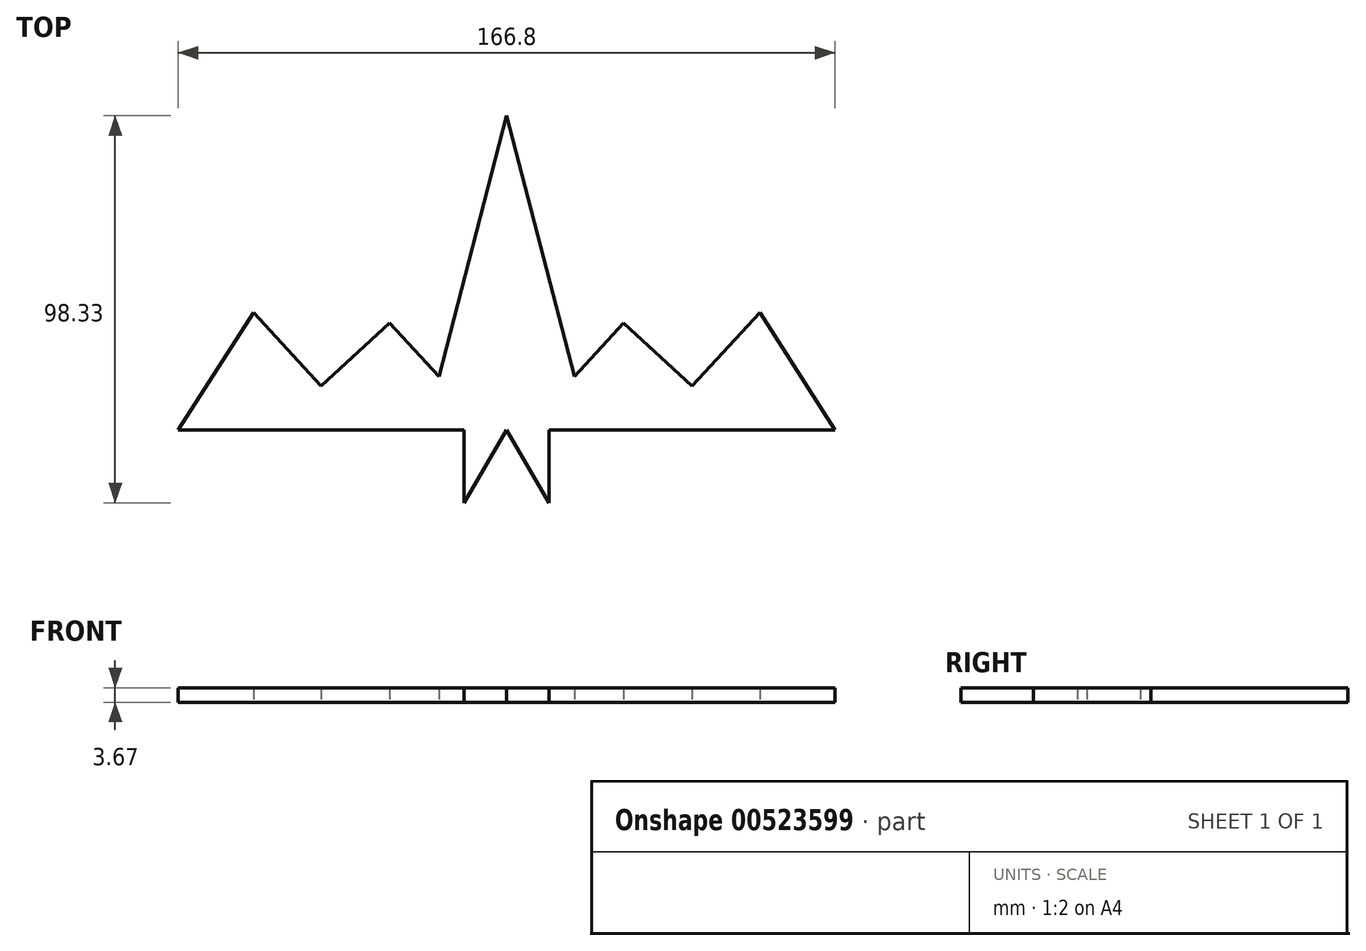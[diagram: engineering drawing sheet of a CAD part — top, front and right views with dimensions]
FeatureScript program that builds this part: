
annotation { "Feature Type Name" : "Feature", "Feature Type Description" : "" }
export const myFeature = defineFeature(function(context is Context, id is Id, definition is map)
    precondition{}
    {
        {
            var Q0;
            Q0=qCreatedBy(makeId("Top.planeOp"),FACE);
            var sketch = newSketch(context, id + "F0", { "sketchPlane" : qUnion([Q0])});
            skLineSegment(sketch, "E0", {"start": v(0, -45.85) * mm, "end": v(-10.79, -64.31) * mm});
            skLineSegment(sketch, "E1", {"start": v(-10.79, -64.31) * mm, "end": v(-10.79, -45.85) * mm});
            skLineSegment(sketch, "E2", {"start": v(-10.79, -45.85) * mm, "end": v(-83.4, -45.85) * mm});
            skLineSegment(sketch, "E3", {"start": v(-83.4, -45.85) * mm, "end": v(-64.31, -15.97) * mm});
            skLineSegment(sketch, "E4", {"start": v(-64.31, -15.97) * mm, "end": v(-47.1, -34.65) * mm});
            skPoint(sketch, "E4.endSnap0", {"position": v(-47.1, -45.85) * mm});
            skLineSegment(sketch, "E5", {"start": v(-47.1, -34.65) * mm, "end": v(-29.76, -18.66) * mm});
            skLineSegment(sketch, "E6", {"start": v(-29.76, -18.66) * mm, "end": v(-17.2, -32.27) * mm});
            skLineSegment(sketch, "E7", {"start": v(-17.2, -32.27) * mm, "end": v(0, 34.02) * mm});
            skLineSegment(sketch, "E8", {"start": v(0, -45.85) * mm, "end": v(0, 34.02) * mm, "construction": true});
            skLineSegment(sketch, "E9.MirrorCS", {"start": v(83.4, -45.85) * mm, "end": v(64.31, -15.97) * mm});
            skLineSegment(sketch, "E10.MirrorCS", {"start": v(64.31, -15.97) * mm, "end": v(47.1, -34.65) * mm});
            skLineSegment(sketch, "E11.MirrorCS", {"start": v(47.1, -34.65) * mm, "end": v(29.76, -18.66) * mm});
            skLineSegment(sketch, "E12.MirrorCS", {"start": v(29.76, -18.66) * mm, "end": v(17.2, -32.27) * mm});
            skLineSegment(sketch, "E13.MirrorCS", {"start": v(17.2, -32.27) * mm, "end": v(0, 34.02) * mm});
            skLineSegment(sketch, "E14.MirrorCS", {"start": v(10.79, -45.85) * mm, "end": v(83.4, -45.85) * mm});
            skLineSegment(sketch, "E15.MirrorCS", {"start": v(0, -45.85) * mm, "end": v(10.79, -64.31) * mm});
            skLineSegment(sketch, "E16.MirrorCS", {"start": v(10.79, -64.31) * mm, "end": v(10.79, -45.85) * mm});
            skSolve(sketch);
        }
        {
            var Q0;
            Q0=makeQuery(id+"F0.imprint","IMPRINT",FACE,{"disambiguationData":[TD([[makeQuery(id+"F0.imprint","IMPRINT",EDGE,{"derivedFrom":sQuery(id+"F0.wireOp",EDGE,"E0")}),-1.0]])]});
            extrude(context, id + "F1", {"entities" : qUnion([Q0]), "depth" : 3.67 * mm, "offsetDistance" : 25.4 * mm});
        }
    });
